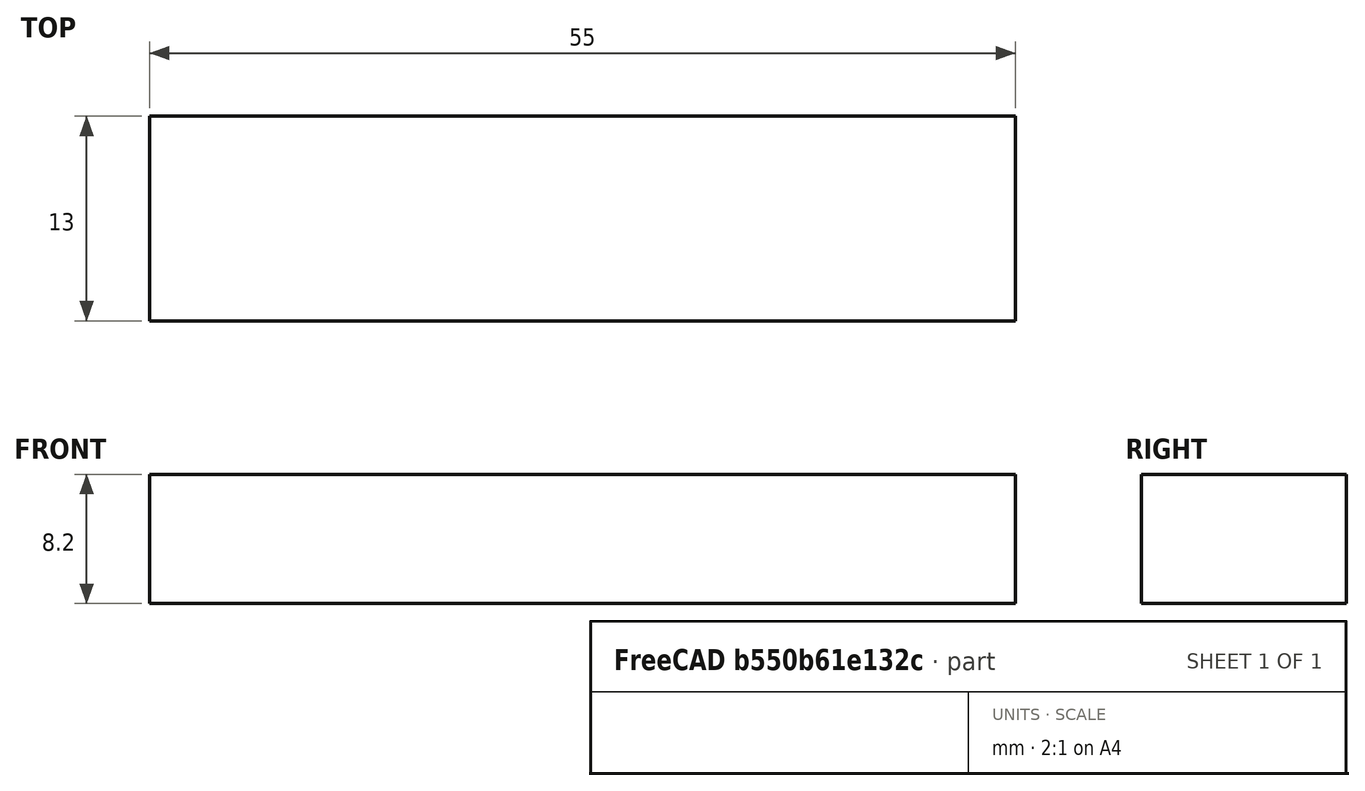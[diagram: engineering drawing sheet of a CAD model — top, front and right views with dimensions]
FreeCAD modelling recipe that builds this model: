
FCSTD DOCUMENT  (FreeCAD 0.18R4 (GitTag))
Label: Archim_board_heatsink
License: CreativeCommons Attribution-ShareAlike
LicenseURL: http://creativecommons.org/licenses/by-sa/4.0/
objects: Drawing::FeatureView×8, Drawing::FeatureViewPart×2, Sketcher::SketchObject×1, PartDesign::Pad×1, PartDesign::Body×1, Drawing::FeaturePage×1
note: 4 computed .brp shape members not serialized (recipe doc carries the construction recipe); baked Part::Feature solids carry a one-line shape summary decoded from their .brp

FEATURE [Sketcher::SketchObject] Sketch
  MapMode = 5
  Support = -> [XY_Plane]
  sketch-geometry (4):
    g0: LineSegment StartX=0 StartY=0 StartZ=0 EndX=55 EndY=0 EndZ=0
    g1: LineSegment StartX=55 StartY=0 StartZ=0 EndX=55 EndY=13 EndZ=0
    g2: LineSegment StartX=55 StartY=13 StartZ=0 EndX=0 EndY=13 EndZ=0
    g3: LineSegment StartX=0 StartY=13 StartZ=0 EndX=0 EndY=0 EndZ=0
  constraints (11):
    c: Coincident(g0,g1)
    c: Coincident(g1,g2)
    c: Coincident(g2,g3)
    c: Coincident(g3,g0)
    c: Horizontal(g0)
    c: Horizontal(g2)
    c: Vertical(g1)
    c: Vertical(g3)
    c: Coincident(g0,g-1)
    c: DistanceY(g3,g3) = 13
    c: DistanceX(g2,g2) = 55
FEATURE [PartDesign::Pad] Pad
  Length = 8.2
  Length2 = 100
  Profile = -> Sketch
  Type = 0
FEATURE [PartDesign::Body] Body
  Group = -> [Sketch,Pad]
  Origin = -> Origin
  Tip = -> Pad
FEATURE [Drawing::FeatureViewPart] Ortho  label="Ortho_0_0"
  Direction = (1,0,0)
  HiddenWidth = 0.15
  LineWidth = 0.35
  Rotation = -90
  Scale = 3
  ShowHiddenLines = false
  ShowSmoothLines = false
  Source = -> Pad
  Tolerance = 0.05
  ViewResult = <g id="Ortho_0_0"\n   transform="rotate(-90,34.3333,95) translate(34.3333,95) scale(3,3)"\n  >\n<g   fill="none"\n   stroke="rgb(0, 0, 0)"\n   stroke-linecap="butt"\n   stroke-linejoin="miter"\n   stroke-width="0.116667"\n   transform="scale(1,-1)"\n  >\n<path id= "1" d=" M 0 0 L 8.2 0 " />\n<path id= "2" d=" M 0 -13 L 8.2 -13 " />\n<path id= "3" d=" M 0 0 L 0 -13 " />\n<path id= "4" d=" M 8.2 0 L 8.2 -13 " />\n</g>\n</g>
  Visible = true
  X = 34.3333
  Y = 95
FEATURE [Drawing::FeatureViewPart] Ortho001  label="Ortho_1_0"
  Direction = (0,1,0)
  HiddenWidth = 0.15
  LineWidth = 0.35
  Rotation = -90
  Scale = 3
  ShowHiddenLines = false
  ShowSmoothLines = false
  Source = -> Pad
  Tolerance = 0.05
  ViewResult = <g id="Ortho_1_0"\n   transform="rotate(-90,262.667,95) translate(262.667,95) scale(3,3)"\n  >\n<g   fill="none"\n   stroke="rgb(0, 0, 0)"\n   stroke-linecap="butt"\n   stroke-linejoin="miter"\n   stroke-width="0.116667"\n   transform="scale(1,-1)"\n  >\n<path id= "1" d=" M 0 55 L 8.2 55 " />\n<path id= "2" d=" M 0 0 L 8.2 0 " />\n<path id= "3" d=" M 0 55 L 0 0 " />\n<path id= "4" d=" M 8.2 55 L 8.2 0 " />\n</g>\n</g>
  Visible = true
  X = 262.667
  Y = 95
FEATURE [Drawing::FeatureView] dim002
  Rotation = 0
  ViewResult = <g> \n  <line x1="34.333300" y1="66.000000" x2="34.333300" y2="60.186322" style="stroke:rgb(0,0,255);stroke-width:0.25" />\n<line x1="73.333300" y1="66.000000" x2="73.333300" y2="60.186322" style="stroke:rgb(0,0,255);stroke-width:0.25" />\n<line x1="34.333300" y1="61.186322" x2="73.333300" y2="61.186322" style="stroke:rgb(0,0,255);stroke-width:0.25" /> \n  <polygon points="73.333300,61.186322 71.333300,60.186322 71.333300,61.186322 71.333300,62.186322" style="fill:rgb(0,0,255);stroke:rgb(0,0,255);stroke-width:0" /><polygon points="34.333300,61.186322 36.333300,62.186322 36.333300,61.186322 36.333300,60.186322" style="fill:rgb(0,0,255);stroke:rgb(0,0,255);stroke-width:0" /> \n  <text x="53.833300" y="59.186322" font-family="inherit" font-size="3" fill="rgb(0,0,255)" text-anchor="middle" transform="rotate(0.000000 53.833300,59.186322)" >13.0 </text> </g>
  Visible = true
  X = 0
  Y = 0
FEATURE [Drawing::FeatureView] dim003
  Rotation = 0
  ViewResult = <g> \n  <line x1="97.667000" y1="66.000000" x2="97.667000" y2="57.548980" style="stroke:rgb(0,0,255);stroke-width:0.25" />\n<line x1="262.667000" y1="66.000000" x2="262.667000" y2="57.548980" style="stroke:rgb(0,0,255);stroke-width:0.25" />\n<line x1="97.667000" y1="58.548980" x2="262.667000" y2="58.548980" style="stroke:rgb(0,0,255);stroke-width:0.25" /> \n  <polygon points="262.667000,58.548980 260.667000,57.548980 260.667000,58.548980 260.667000,59.548980" style="fill:rgb(0,0,255);stroke:rgb(0,0,255);stroke-width:0" /><polygon points="97.667000,58.548980 99.667000,59.548980 99.667000,58.548980 99.667000,57.548980" style="fill:rgb(0,0,255);stroke:rgb(0,0,255);stroke-width:0" /> \n  <text x="180.167000" y="56.548980" font-family="inherit" font-size="3" fill="rgb(0,0,255)" text-anchor="middle" transform="rotate(0.000000 180.167000,56.548980)" >55.0 </text> </g>
  Visible = true
  X = 0
  Y = 0
FEATURE [Drawing::FeatureView] dimText001
  Rotation = 0
  ViewResult = <g> <text x="195.427001" y="10.021898" font-family="inherit" font-size="3" fill="rgb(0,0,0)" text-anchor="inherit" transform="rotate(0.000000 195.427001,10.021898)" >Notes</text> </g>
  Visible = true
  X = 0
  Y = 0
FEATURE [Drawing::FeatureView] dimText002
  Rotation = 0
  ViewResult = <g> <text x="194.108331" y="14.505378" font-family="inherit" font-size="3" fill="rgb(0,0,0)" text-anchor="inherit" transform="rotate(0.000000 194.108331,14.505378)" >1. Parts must be RoHS compliant</text> </g>
  Visible = true
  X = 0
  Y = 0
FEATURE [Drawing::FeatureView] dimText003
  Rotation = 0
  ViewResult = <g> <text x="194.108331" y="18.725124" font-family="inherit" font-size="3" fill="rgb(0,0,0)" text-anchor="inherit" transform="rotate(0.000000 194.108331,18.725124)" >2. Parts must be clean, free of oil and debris</text> </g>
  Visible = true
  X = 0
  Y = 0
FEATURE [Drawing::FeatureView] dimText004
  Rotation = 0
  ViewResult = <g> <text x="194.108331" y="22.944871" font-family="inherit" font-size="3" fill="rgb(0,0,0)" text-anchor="inherit" transform="rotate(0.000000 194.108331,22.944871)" >3. Break all edges</text> </g>
  Visible = true
  X = 0
  Y = 0
FEATURE [Drawing::FeatureView] dimText005
  Rotation = 0
  ViewResult = <g> <text x="194.108331" y="26.900883" font-family="inherit" font-size="3" fill="rgb(0,0,0)" text-anchor="inherit" transform="rotate(0.000000 194.108331,26.900883)" >4. Material: 6061 Aluminum</text> </g>
  Visible = true
  X = 0
  Y = 0
FEATURE [Drawing::FeatureView] dim001
  Rotation = 0
  ViewResult = <g> \n  <line x1="32.333300" y1="95.000000" x2="25.605659" y2="95.000000" style="stroke:rgb(0,0,255);stroke-width:0.25" />\n<line x1="32.333300" y1="70.400000" x2="25.605659" y2="70.400000" style="stroke:rgb(0,0,255);stroke-width:0.25" />\n<line x1="26.605659" y1="95.000000" x2="26.605659" y2="70.400000" style="stroke:rgb(0,0,255);stroke-width:0.25" /> \n  <polygon points="26.605659,70.400000 25.605659,72.400000 26.605659,72.400000 27.605659,72.400000" style="fill:rgb(0,0,255);stroke:rgb(0,0,255);stroke-width:0" /><polygon points="26.605659,95.000000 27.605659,93.000000 26.605659,93.000000 25.605659,93.000000" style="fill:rgb(0,0,255);stroke:rgb(0,0,255);stroke-width:0" /> \n  <text x="24.605659" y="82.700000" font-family="inherit" font-size="3" fill="rgb(0,0,255)" text-anchor="middle" transform="rotate(-90.000000 24.605659,82.700000)" >8.2 </text> </g>
  Visible = true
  X = 0
  Y = 0
FEATURE [Drawing::FeaturePage] Page
  EditableTexts = West | 01/14/2020 | CHECKED | XX/XX/XXXX | Machined Part, Archim Heatsink, Syn1 | 100064 | 6061 Aluminum | IR | 1 OF 1
  Group = -> [Ortho,Ortho001,dim002,dim003,dimText001,dimText002,dimText003,dimText004,dimText005,dim001]
  Template = <userpath>/Desktop/drawing templates/A4_Page1_attribution.svg
